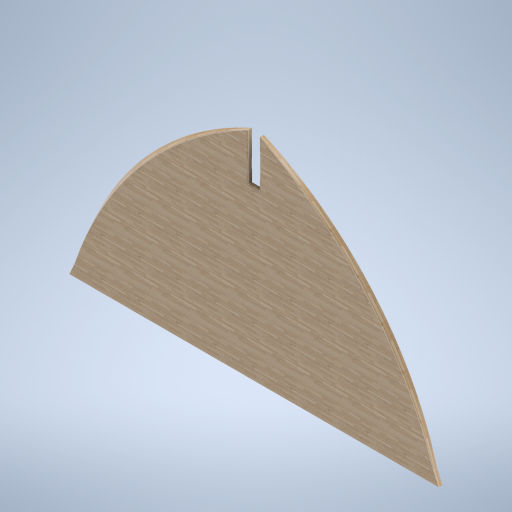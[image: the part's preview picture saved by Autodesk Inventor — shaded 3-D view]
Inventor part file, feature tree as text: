
AUTODESK INVENTOR PART (.ipt)
format: ipt  version: 2024.2 (Build 282272000, 272)  size: 365,056 bytes
history: native  units: mm
features: sketch x2, plane x2, loft x1
ambient origin geometry x8: Origin, YZ Plane, XZ Plane, XY Plane, X Axis, Y Axis, Z Axis, Center Point
bodies: Solid1 (feature_tree)
feature tree (5):
  sketch  "Sketch1"  dims[d2=0.0mm d3=-100.0mm d5=7.0mm]
  plane  "Work Plane2"
  loft  "Loft1"
  plane  "Work Plane1"
  sketch  "Sketch3"  dims[d6=0.0mm d7=90.0deg d8=0.0mm d9=90.0deg]
